# Revit family: Shower-Showerhead-KOHLER-Flipside-K-45427_1
name_source: partatom
category: Plumbing Fixtures
revit_build: Autodesk Revit 2017 (Build: 20160225_1515(x64)
units: mm (PartAtom-declared; Revit-internal decimal feet)

## family parameters
Cut with Voids When Loaded = No
Host = Face
OmniClass Number = 23.31.17.00
OmniClass Title = Showers
Part Type = Normal
Room Calculation Point = No
Round Connector Dimension = Use Diameter
Shared = No

## types (4) — shared parameters
ADA Compliant = No
Assembly Code = D2010700
CW Connection = No
Cold Water Inlet = Cold Water Inlet
Date Modified = 02/02/2021
Default Elevation = 0"
Description = 1.75 GPM Multifunction Showerhead
Drain Included = No
Flow Rate = 2 GPM
HW Connection = Yes
Height = 5 5/16"
Hot Water Inlet = Hot Water Inlet
Length = 5 3/8"
Manufacturer = KOHLER Co.
Master Format 2014 = 22 42 23
Master Format 2014 Name = Residential Showers
Material = Premium Metal Construction
Panel Thickness = 0"
Pressure = 0.00 psi
Product Documentation Link = https://www.us.kohler.com
Product Name = Flipside
Product Page URL = http://www.us.kohler.com
Tempered Water Inlet = Tempered Water Inlet
URL = https://www.us.kohler.com
Vent Connection = No
Waste Connection = No
Waste Water Outlet = Waste Water Outlet
WaterSense Certified = Yes
Width = 5 3/8"

## per-type parameters (varying)
| type | Finish | Model | Type |
| CP-Polished Chrome | Kohler-Metal-CP-Polished_Chrome | K-45427-G-CP | 1 |
| SN-Vibrant Polished Nickel | Kohler-Metal-SN-Vibrant_Polished_Nickel | K-45427-G-SN | 2 |
| BN-Vibrant Brushed Nickel | Kohler-Metal-BN-Vibrant_Brushed_Nickel | K-45427-G-BN | 3 |
| 2BZ-Oil-Rubbed Bronze | Kohler-Metal-2BZ-Oil_Rubbed_Bronze | K-45427-G-2BZ | 4 |

## geometry (parser evidence)
native form markers: Sweep x4
no freeform markers — native parametric forms only
